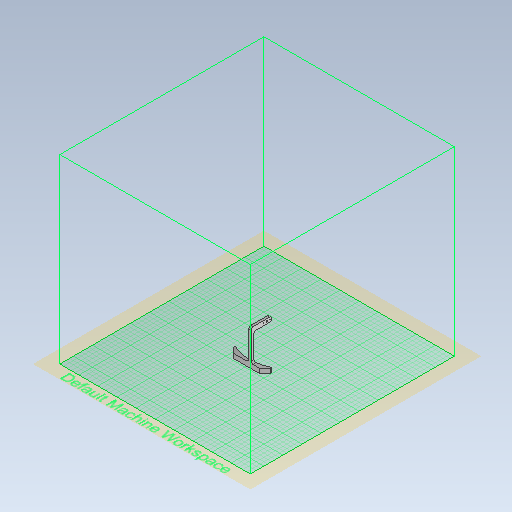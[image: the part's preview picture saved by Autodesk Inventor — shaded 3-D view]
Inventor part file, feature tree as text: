
AUTODESK INVENTOR PART (.ipt)
format: ipt  version: 2020 (Build 240168000, 168)  size: 348,672 bytes
history: native  units: mm
features: extrude x5, sketch x3, chamfer x2, fillet x2
ambient origin geometry x8: Origin, YZ Plane, XZ Plane, XY Plane, X Axis, Y Axis, Z Axis, Center Point
bodies: Solide1 (feature_tree)
feature tree (12):
  extrude  "Extrusion1"  Depth=15.0mm
  extrude  "Extrusion2"  Depth=80.0mm
  extrude  "Extrusion5"  Depth=10.0mm TaperAngle=0.0deg
  extrude  "Extrusion6"  Depth=5.0mm
  chamfer  "Chanfrein1"  Distance=80.0mm
  fillet  "Congé1"  Radius=6.0mm
  fillet  "Congé2"  Radius=67.9mm
  chamfer  "Chanfrein2"  Distance=4.6mm
  extrude  "Extrusion8"  Depth=6.0mm
  sketch  "Esquisse1"
  sketch  "Esquisse2"
  sketch  "Esquisse6"
